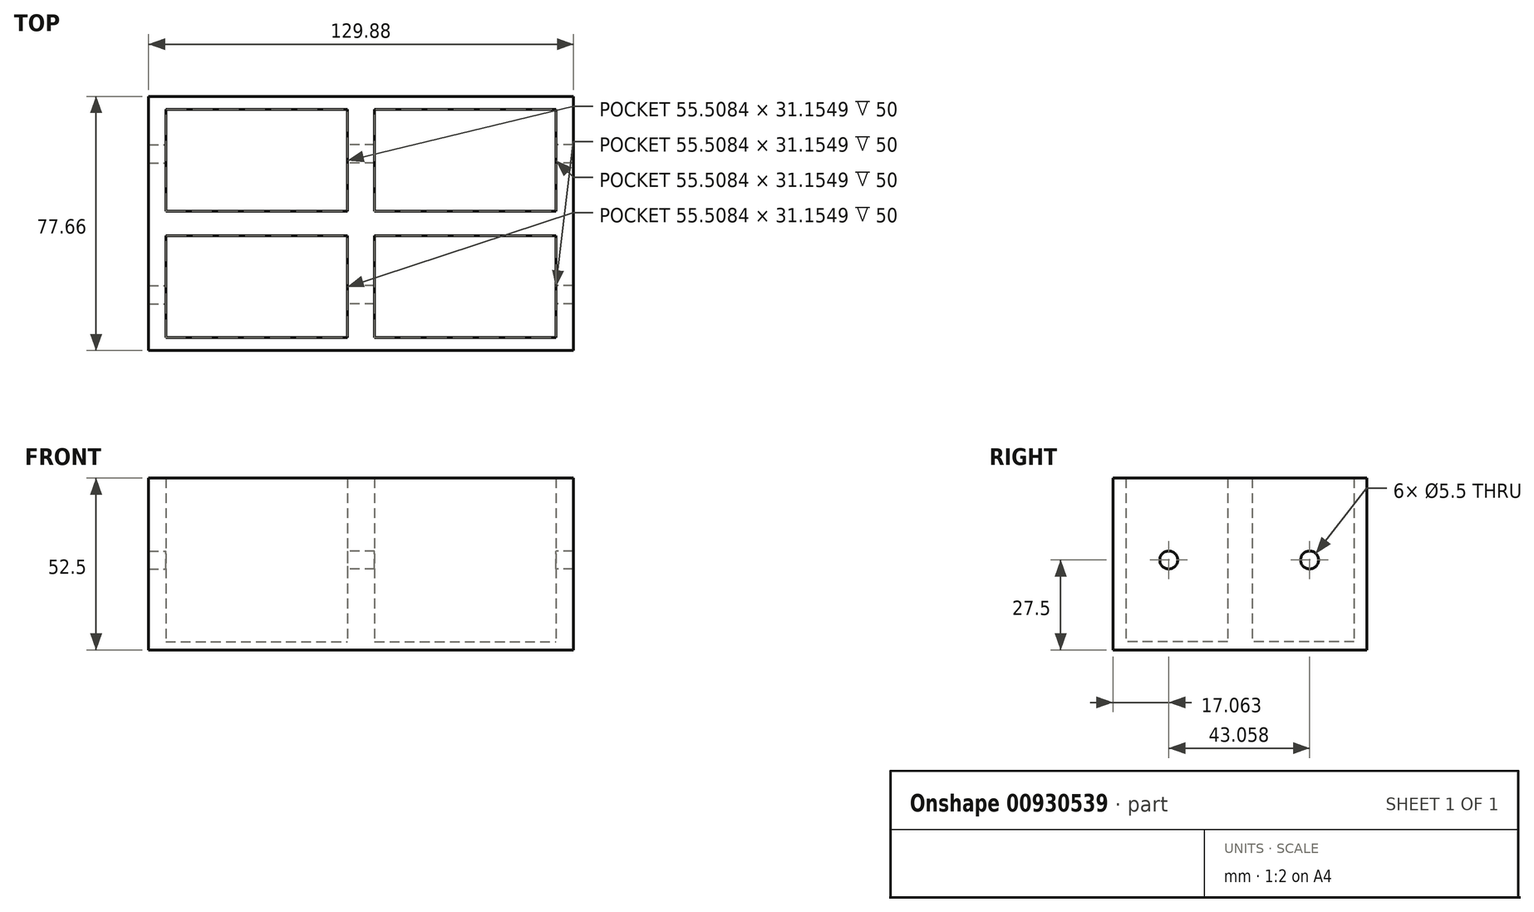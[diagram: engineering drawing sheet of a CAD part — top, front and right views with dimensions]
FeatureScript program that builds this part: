
annotation { "Feature Type Name" : "Feature", "Feature Type Description" : "" }
export const myFeature = defineFeature(function(context is Context, id is Id, definition is map)
    precondition{}
    {
        {
            var Q0;
            Q0=qCreatedBy(makeId("Top.planeOp"),FACE);
            var sketch = newSketch(context, id + "F0", { "sketchPlane" : qUnion([Q0])});
            skLineSegment(sketch, "E0.bottom", {"start": v(-64.94, 38.83) * mm, "end": v(64.94, 38.83) * mm});
            skLineSegment(sketch, "E0.top", {"start": v(-64.94, -38.83) * mm, "end": v(64.94, -38.83) * mm});
            skLineSegment(sketch, "E0.left", {"start": v(-64.94, 38.83) * mm, "end": v(-64.94, -38.83) * mm});
            skLineSegment(sketch, "E0.right", {"start": v(64.94, 38.83) * mm, "end": v(64.94, -38.83) * mm});
            skPoint(sketch, "E0.middle", {"position": v(0, 0) * mm});
            skLineSegment(sketch, "E1.bottom", {"start": v(-59.68, 34.88) * mm, "end": v(59.68, 34.88) * mm});
            skLineSegment(sketch, "E1.top", {"start": v(-59.68, -34.88) * mm, "end": v(59.68, -34.88) * mm});
            skLineSegment(sketch, "E1.left", {"start": v(-59.68, 34.88) * mm, "end": v(-59.68, -34.88) * mm});
            skLineSegment(sketch, "E1.right", {"start": v(59.68, 34.88) * mm, "end": v(59.68, -34.88) * mm});
            skLineSegment(sketch, "E2", {"start": v(-72.84, 0) * mm, "end": v(75.04, 0) * mm, "construction": true});
            skPoint(sketch, "E2.endSnap0", {"position": v(64.94, 0) * mm});
            skLineSegment(sketch, "E3", {"start": v(-4.17, 34.88) * mm, "end": v(-4.17, -34.88) * mm});
            skLineSegment(sketch, "E4", {"start": v(4.17, 34.88) * mm, "end": v(4.17, -34.88) * mm});
            skLineSegment(sketch, "E5", {"start": v(-59.68, 3.73) * mm, "end": v(-4.17, 3.73) * mm});
            skLineSegment(sketch, "E6", {"start": v(4.17, 3.73) * mm, "end": v(59.68, 3.73) * mm});
            skLineSegment(sketch, "E7", {"start": v(-59.68, -3.73) * mm, "end": v(-4.17, -3.73) * mm});
            skLineSegment(sketch, "E8", {"start": v(4.17, -3.73) * mm, "end": v(59.68, -3.73) * mm});
            skSolve(sketch);
        }
        {
            var Q0;
            Q0 = qSketchRegion(id + "F0", true);
            var Q1;
            {var subQ0=sQuery(id+"F0.wireOp",EDGE,"E6");Q1=makeQuery(id+"F0.imprint","IMPRINT",FACE,{"disambiguationData":[TD([[makeQuery(id+"F0.imprint","IMPRINT",EDGE,{"derivedFrom":subQ0}),-1.0]])]});}
            var Q2;
            {var subQ0=sQuery(id+"F0.wireOp",EDGE,"E5");Q2=makeQuery(id+"F0.imprint","IMPRINT",FACE,{"disambiguationData":[TD([[makeQuery(id+"F0.imprint","IMPRINT",EDGE,{"derivedFrom":subQ0}),-1.0]])]});}
            var Q3;
            {var subQ0=sQuery(id+"F0.wireOp",EDGE,"E3");var subQ3=sQuery(id+"F0.wireOp",EDGE,"E1.bottom");var subQ4=makeQuery(id+"F0.imprint","INTERSECT",VERTEX,{"derivedFrom":[subQ3,subQ0]});Q3=makeQuery(id+"F0.imprint","IMPRINT",FACE,{"disambiguationData":[TD([[makeQuery(id+"F0.imprint","IMPRINT",EDGE,{"disambiguationData":[TD([[subQ4,-1.0]])],"derivedFrom":subQ3}),-1.0]])]});}
            extrude(context, id + "F1", {"entities" : qUnion([Q0, Q1, Q2, Q3]), "depth" : 50 * mm, "offsetDistance" : 25 * mm});
        }
        {
            var Q0;
            Q0=makeQuery(id+"F0.imprint","IMPRINT",FACE,{"disambiguationData":[TD([[makeQuery(id+"F0.imprint","IMPRINT",EDGE,{"derivedFrom":sQuery(id+"F0.wireOp",EDGE,"E0.bottom")}),-1.0]])]});
            var Q1;
            {var subQ5=sQuery(id+"F0.wireOp",EDGE,"E7");Q1=makeQuery(id+"F0.imprint","IMPRINT",FACE,{"disambiguationData":[TD([[makeQuery(id+"F0.imprint","IMPRINT",EDGE,{"derivedFrom":subQ5}),-1.0]])]});}
            var Q2;
            {var subQ5=sQuery(id+"F0.wireOp",EDGE,"E5");Q2=makeQuery(id+"F0.imprint","IMPRINT",FACE,{"disambiguationData":[TD([[makeQuery(id+"F0.imprint","IMPRINT",EDGE,{"derivedFrom":subQ5}),1.0]])]});}
            var Q3;
            {var subQ5=sQuery(id+"F0.wireOp",EDGE,"E8");Q3=makeQuery(id+"F0.imprint","IMPRINT",FACE,{"disambiguationData":[TD([[makeQuery(id+"F0.imprint","IMPRINT",EDGE,{"derivedFrom":subQ5}),-1.0]])]});}
            var Q4;
            {var subQ5=sQuery(id+"F0.wireOp",EDGE,"E6");Q4=makeQuery(id+"F0.imprint","IMPRINT",FACE,{"disambiguationData":[TD([[makeQuery(id+"F0.imprint","IMPRINT",EDGE,{"derivedFrom":subQ5}),1.0]])]});}
            var Q5;
            {var subQ0=sQuery(id+"F0.wireOp",EDGE,"E6");Q5=makeQuery(id+"F0.imprint","IMPRINT",FACE,{"disambiguationData":[TD([[makeQuery(id+"F0.imprint","IMPRINT",EDGE,{"derivedFrom":subQ0}),-1.0]])]});}
            var Q6;
            {var subQ0=sQuery(id+"F0.wireOp",EDGE,"E3");var subQ3=sQuery(id+"F0.wireOp",EDGE,"E1.bottom");var subQ4=makeQuery(id+"F0.imprint","INTERSECT",VERTEX,{"derivedFrom":[subQ3,subQ0]});Q6=makeQuery(id+"F0.imprint","IMPRINT",FACE,{"disambiguationData":[TD([[makeQuery(id+"F0.imprint","IMPRINT",EDGE,{"disambiguationData":[TD([[subQ4,-1.0]])],"derivedFrom":subQ3}),-1.0]])]});}
            var Q7;
            {var subQ0=sQuery(id+"F0.wireOp",EDGE,"E5");Q7=makeQuery(id+"F0.imprint","IMPRINT",FACE,{"disambiguationData":[TD([[makeQuery(id+"F0.imprint","IMPRINT",EDGE,{"derivedFrom":subQ0}),-1.0]])]});}
            extrude(context, id + "F2", {"entities" : qUnion([Q0, Q1, Q2, Q3, Q4, Q5, Q6, Q7]), "operationType" : NewBodyOperationType.ADD, "oppositeDirection" : true, "depth" : 2.5 * mm, "offsetDistance" : 25 * mm});
        }
        {
            var Q0;
            {var subQ0=sQuery(id+"F0.wireOp",EDGE,"E3");Q0=makeQuery(id+"F1.opExtrude","SWEPT_FACE",FACE,{"disambiguationData":[OSD([subQ0]),TDD([makeQuery(id+"F0.imprint","IMPRINT",EDGE,{"disambiguationData":[TD([[makeQuery(id+"F0.imprint","INTERSECT",VERTEX,{"derivedFrom":[sQuery(id+"F0.wireOp",EDGE,"E1.bottom"),subQ0]}),-1.0]])],"derivedFrom":subQ0})])]});}
            var sketch = newSketch(context, id + "F3", { "sketchPlane" : qUnion([Q0])});
            skPoint(sketch, "E9.positionSnap0", {"position": v(-3.73, 25) * mm});
            skLineSegment(sketch, "E10", {"start": v(-74.26, 25) * mm, "end": v(60.86, 25) * mm, "construction": true});
            skPoint(sketch, "E11", {"position": v(-21.3, 25) * mm});
            skPoint(sketch, "E12", {"position": v(21.77, 25) * mm});
            skCircle(sketch, "E13", {"center": v(-21.3, 25) * mm, "radius": 7.01 * mm});
            skCircle(sketch, "E14", {"center": v(21.77, 25) * mm, "radius": 7.01 * mm});
            skSolve(sketch);
        }
        {
            var Q0;
            Q0=sQuery(id+"F3.wireOp",VERTEX,"E14.center");
            var Q1;
            Q1=sQuery(id+"F3.wireOp",VERTEX,"E11");
            var Q2;
            Q2=makeQuery(id+"F1.opExtrude","SWEPT_BODY",BODY,{"disambiguationData":[OSD([sQuery(id+"F0.wireOp",EDGE,"E0.bottom"),sQuery(id+"F0.wireOp",EDGE,"E0.top"),sQuery(id+"F0.wireOp",EDGE,"E0.left"),sQuery(id+"F0.wireOp",EDGE,"E0.right"),sQuery(id+"F0.wireOp",EDGE,"E1.bottom"),sQuery(id+"F0.wireOp",EDGE,"E1.top"),sQuery(id+"F0.wireOp",EDGE,"E1.left"),sQuery(id+"F0.wireOp",EDGE,"E1.right"),sQuery(id+"F0.wireOp",EDGE,"E3"),sQuery(id+"F0.wireOp",EDGE,"E4"),sQuery(id+"F0.wireOp",EDGE,"E5"),sQuery(id+"F0.wireOp",EDGE,"E6"),sQuery(id+"F0.wireOp",EDGE,"E7"),sQuery(id+"F0.wireOp",EDGE,"E8")])]});
            hole(context, id + "F4", {"style" : HoleStyle.SIMPLE, "endStyle" : HoleEndStyle.THROUGH, "standardTappedOrClearance" : lookupTablePath({ "fit" : "Normal", "standard" : "ISO", "size" : "M5", "type" : "Clearance" }), "standardBlindInLast" : lookupTablePath({ "fit" : "Normal", "standard" : "ISO", "engagement" : "75%", "pitch" : "0.8 mm", "size" : "M5", "type" : "Clearance & tapped" }), "holeDiameter" : 5.5 * mm, "majorDiameter" : 5 * mm, "isTappedThrough" : true, "tappedDepth" : 12 * mm, "tapClearance" : 3, "locations" : qUnion([Q0, Q1]), "scope" : qUnion([Q2])});
        }
        {
            var Q0;
            Q0=sQuery(id+"F3.wireOp",VERTEX,"E13.center");
            var Q1;
            Q1=sQuery(id+"F3.wireOp",VERTEX,"E14.center");
            var Q2;
            Q2=makeQuery(id+"F1.opExtrude","SWEPT_BODY",BODY,{"disambiguationData":[OSD([sQuery(id+"F0.wireOp",EDGE,"E0.bottom"),sQuery(id+"F0.wireOp",EDGE,"E0.top"),sQuery(id+"F0.wireOp",EDGE,"E0.left"),sQuery(id+"F0.wireOp",EDGE,"E0.right"),sQuery(id+"F0.wireOp",EDGE,"E1.bottom"),sQuery(id+"F0.wireOp",EDGE,"E1.top"),sQuery(id+"F0.wireOp",EDGE,"E1.left"),sQuery(id+"F0.wireOp",EDGE,"E1.right"),sQuery(id+"F0.wireOp",EDGE,"E3"),sQuery(id+"F0.wireOp",EDGE,"E4"),sQuery(id+"F0.wireOp",EDGE,"E5"),sQuery(id+"F0.wireOp",EDGE,"E6"),sQuery(id+"F0.wireOp",EDGE,"E7"),sQuery(id+"F0.wireOp",EDGE,"E8")])]});
            hole(context, id + "F5", {"style" : HoleStyle.SIMPLE, "endStyle" : HoleEndStyle.THROUGH, "oppositeDirection" : true, "standardTappedOrClearance" : lookupTablePath({ "fit" : "Normal", "standard" : "ISO", "size" : "M5", "type" : "Clearance" }), "standardBlindInLast" : lookupTablePath({ "fit" : "Normal", "standard" : "ISO", "engagement" : "75%", "pitch" : "0.8 mm", "size" : "M5", "type" : "Clearance & tapped" }), "holeDiameter" : 5.5 * mm, "majorDiameter" : 5 * mm, "isTappedThrough" : true, "tappedDepth" : 12 * mm, "tapClearance" : 3, "locations" : qUnion([Q0, Q1]), "scope" : qUnion([Q2])});
        }
    });
